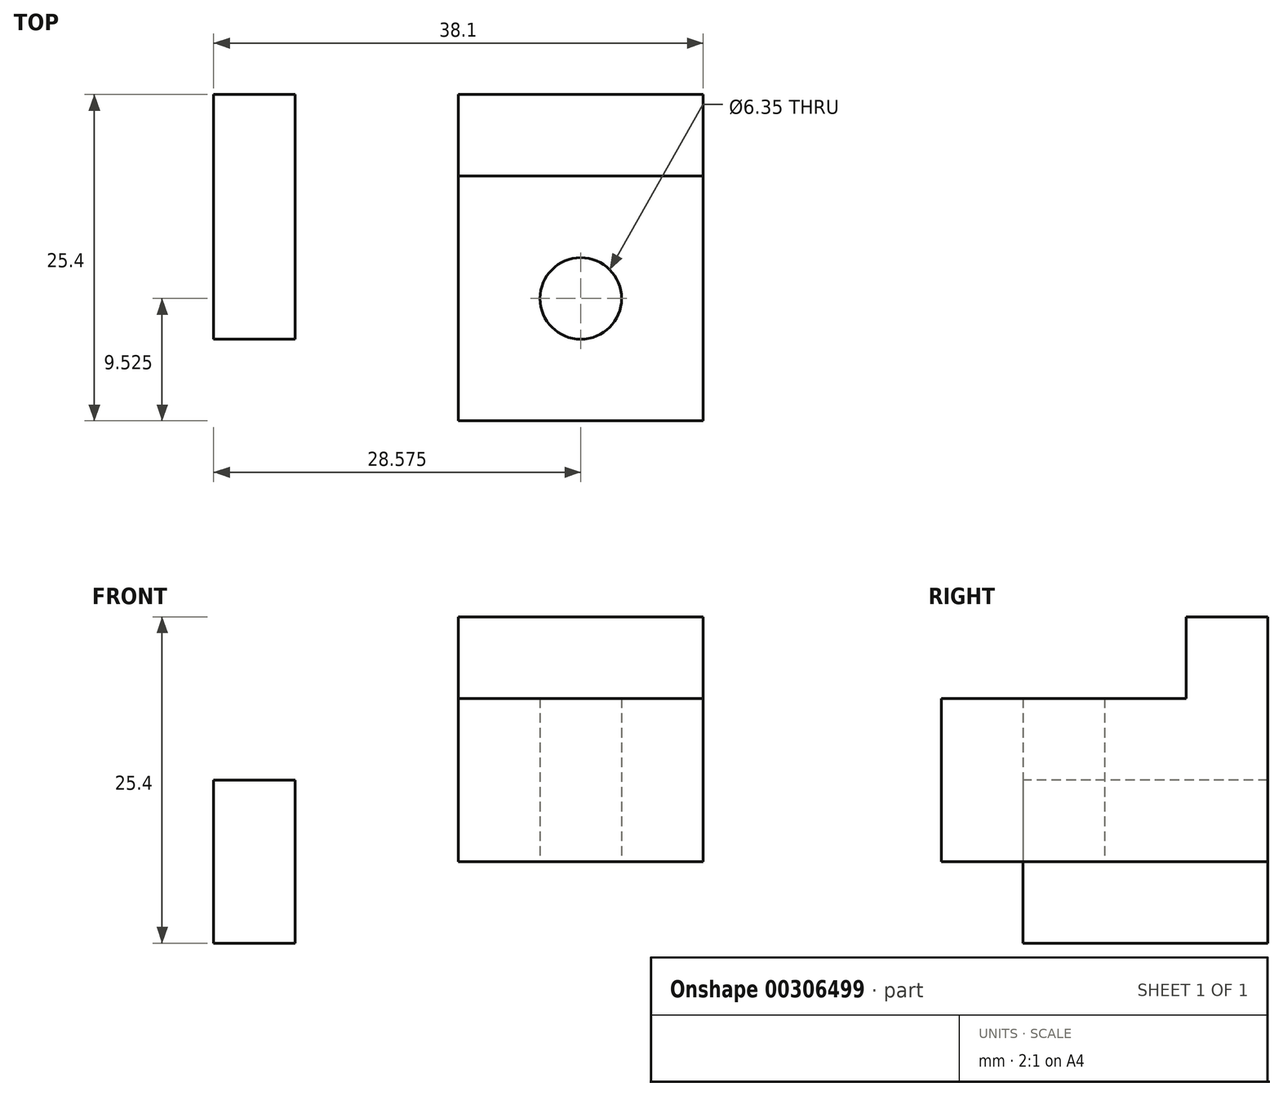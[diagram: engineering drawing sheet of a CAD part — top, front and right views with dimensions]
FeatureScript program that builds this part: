
annotation { "Feature Type Name" : "Feature", "Feature Type Description" : "" }
export const myFeature = defineFeature(function(context is Context, id is Id, definition is map)
    precondition{}
    {
        {
            var Q0;
            Q0=qCreatedBy(makeId("Top.planeOp"),FACE);
            var sketch = newSketch(context, id + "F0", { "sketchPlane" : qUnion([Q0])});
            skLineSegment(sketch, "E0.bottom", {"start": v(-19.05, 19.05) * mm, "end": v(0, 19.05) * mm});
            skLineSegment(sketch, "E0.top", {"start": v(-19.05, 0) * mm, "end": v(0, 0) * mm});
            skLineSegment(sketch, "E0.left", {"start": v(-19.05, 19.05) * mm, "end": v(-19.05, 0) * mm});
            skLineSegment(sketch, "E0.right", {"start": v(0, 19.05) * mm, "end": v(0, 0) * mm});
            skLineSegment(sketch, "E1.bottom", {"start": v(0, 12.7) * mm, "end": v(19.05, 12.7) * mm});
            skLineSegment(sketch, "E1.top", {"start": v(0, -6.35) * mm, "end": v(19.05, -6.35) * mm});
            skLineSegment(sketch, "E1.left", {"start": v(0, 12.7) * mm, "end": v(0, -6.35) * mm});
            skLineSegment(sketch, "E1.right", {"start": v(19.05, 12.7) * mm, "end": v(19.05, -6.35) * mm});
            skLineSegment(sketch, "E2", {"start": v(0, 0) * mm, "end": v(0, -6.35) * mm, "construction": true});
            skLineSegment(sketch, "E3", {"start": v(0, 19.05) * mm, "end": v(19.05, 19.05) * mm});
            skLineSegment(sketch, "E4", {"start": v(19.05, 19.05) * mm, "end": v(19.05, 12.7) * mm});
            skLineSegment(sketch, "E5", {"start": v(-19.05, 19.05) * mm, "end": v(-12.7, 19.05) * mm});
            skLineSegment(sketch, "E6", {"start": v(0, 19.05) * mm, "end": v(-6.35, 19.05) * mm});
            skLineSegment(sketch, "E7", {"start": v(-12.7, 19.05) * mm, "end": v(-12.7, 0) * mm});
            skCircle(sketch, "E8", {"center": v(-6.35, 9.52) * mm, "radius": 3.18 * mm});
            skPoint(sketch, "E9", {"position": v(9.52, -6.35) * mm});
            skPoint(sketch, "E10", {"position": v(19.05, 3.17) * mm});
            skLineSegment(sketch, "E11", {"start": v(9.52, -6.35) * mm, "end": v(9.52, 3.17) * mm, "construction": true});
            skLineSegment(sketch, "E12", {"start": v(9.52, 3.17) * mm, "end": v(19.05, 3.17) * mm, "construction": true});
            skCircle(sketch, "E13", {"center": v(9.52, 3.17) * mm, "radius": 3.18 * mm});
            skSolve(sketch);
        }
        {
            var Q0;
            Q0=makeQuery(id+"F0.imprint","IMPRINT",FACE,{"disambiguationData":[TD([[makeQuery(id+"F0.imprint","IMPRINT",EDGE,{"derivedFrom":sQuery(id+"F0.wireOp",EDGE,"E0.bottom")}),-1.0]])]});
            var Q1;
            {var subQ0=sQuery(id+"F0.wireOp",EDGE,"E0.left");Q1=makeQuery(id+"F0.imprint","IMPRINT",FACE,{"disambiguationData":[TD([[makeQuery(id+"F0.imprint","IMPRINT",EDGE,{"derivedFrom":subQ0}),1.0]])]});}
            extrude(context, id + "F1", {"entities" : qUnion([Q0, Q1]), "depth" : 6.35 * mm});
        }
        {
            var Q0;
            {var subQ3=sQuery(id+"F0.wireOp",EDGE,"E1.bottom");Q0=makeQuery(id+"F0.imprint","IMPRINT",FACE,{"disambiguationData":[TD([[makeQuery(id+"F0.imprint","IMPRINT",EDGE,{"derivedFrom":subQ3}),-1.0]])]});}
            extrude(context, id + "F2", {"entities" : qUnion([Q0]), "operationType" : NewBodyOperationType.ADD, "depth" : 12.7 * mm});
        }
        {
            var Q0;
            Q0=makeQuery(id+"F0.imprint","IMPRINT",FACE,{"disambiguationData":[TD([[makeQuery(id+"F0.imprint","IMPRINT",EDGE,{"derivedFrom":sQuery(id+"F0.wireOp",EDGE,"E0.right")}),1.0]])]});
            extrude(context, id + "F3", {"entities" : qUnion([Q0]), "operationType" : NewBodyOperationType.ADD, "depth" : 19.05 * mm});
        }
        {
            var Q0;
            {var subQ0=sQuery(id+"F0.wireOp",EDGE,"E0.left");Q0=makeQuery(id+"F0.imprint","IMPRINT",FACE,{"disambiguationData":[TD([[makeQuery(id+"F0.imprint","IMPRINT",EDGE,{"derivedFrom":subQ0}),1.0]])]});}
            extrude(context, id + "F4", {"entities" : qUnion([Q0]), "operationType" : NewBodyOperationType.ADD, "oppositeDirection" : true, "depth" : 6.35 * mm});
        }
    });
